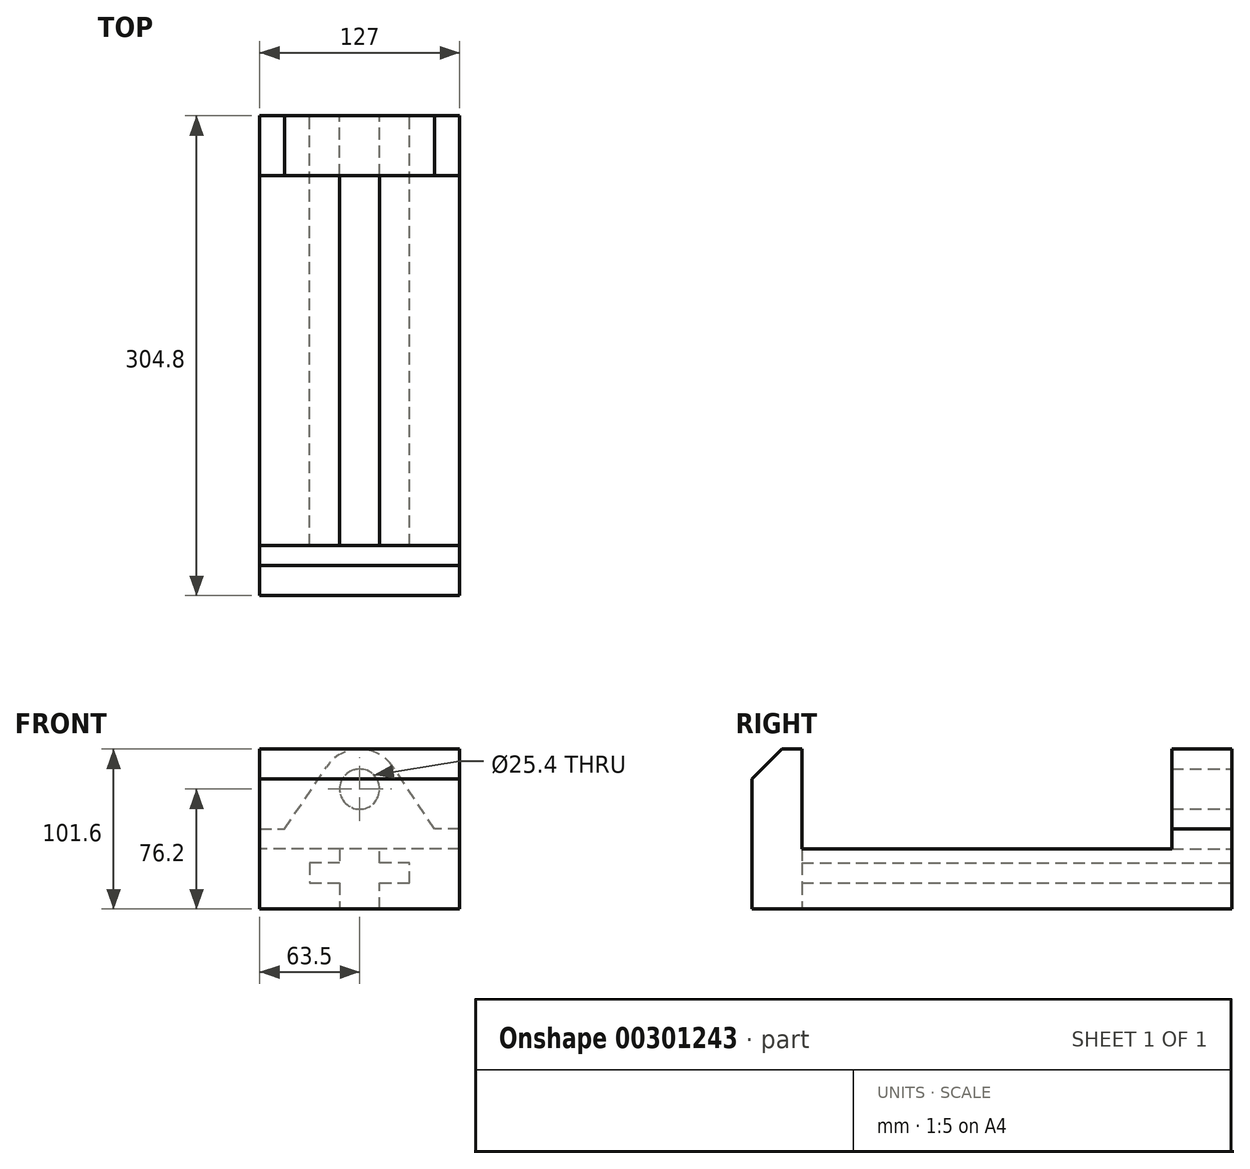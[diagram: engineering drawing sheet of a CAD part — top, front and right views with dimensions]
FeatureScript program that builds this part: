
annotation { "Feature Type Name" : "Feature", "Feature Type Description" : "" }
export const myFeature = defineFeature(function(context is Context, id is Id, definition is map)
    precondition{}
    {
        {
            var Q0;
            Q0=qCreatedBy(makeId("Right.planeOp"),FACE);
            var sketch = newSketch(context, id + "F0", { "sketchPlane" : qUnion([Q0])});
            skLineSegment(sketch, "E0", {"start": v(0, 0) * mm, "end": v(0, 101.6) * mm});
            skLineSegment(sketch, "E1", {"start": v(0, 101.6) * mm, "end": v(31.75, 101.6) * mm});
            skLineSegment(sketch, "E2", {"start": v(31.75, 101.6) * mm, "end": v(31.75, 38.1) * mm});
            skLineSegment(sketch, "E3", {"start": v(31.75, 38.1) * mm, "end": v(266.7, 38.1) * mm});
            skLineSegment(sketch, "E4", {"start": v(266.7, 38.1) * mm, "end": v(266.7, 101.6) * mm});
            skLineSegment(sketch, "E5", {"start": v(266.7, 101.6) * mm, "end": v(304.8, 101.6) * mm});
            skLineSegment(sketch, "E6", {"start": v(304.8, 101.6) * mm, "end": v(304.8, 0) * mm});
            skLineSegment(sketch, "E7", {"start": v(304.8, 0) * mm, "end": v(0, 0) * mm});
            skSolve(sketch);
        }
        {
            var Q0;
            Q0 = qSketchRegion(id + "F0", true);
            extrude(context, id + "F1", {"entities" : qUnion([Q0]), "endBound" : BoundingType.SYMMETRIC, "depth" : 127 * mm});
        }
        {
            var Q0;
            Q0=makeQuery(id+"F1.opExtrude","SWEPT_FACE",FACE,{"disambiguationData":[OSD([sQuery(id+"F0.wireOp",EDGE,"E6")])]});
            var sketch = newSketch(context, id + "F2", { "sketchPlane" : qUnion([Q0])});
            skLineSegment(sketch, "E8", {"start": v(-63.5, 50.8) * mm, "end": v(-47.63, 50.8) * mm});
            skLineSegment(sketch, "E9", {"start": v(-47.63, 50.8) * mm, "end": v(-21.1, 90.35) * mm});
            skLineSegment(sketch, "E10", {"start": v(63.5, 50.8) * mm, "end": v(47.63, 50.8) * mm});
            skPoint(sketch, "E10.endSnap0", {"position": v(63.5, 50.8) * mm});
            skLineSegment(sketch, "E11", {"start": v(47.63, 50.8) * mm, "end": v(21.1, 90.35) * mm});
            skArc(sketch, "E12", {"start": v(-21.1, 90.35) * mm, "mid": v(0, 101.6) * mm, "end": v(21.1, 90.35) * mm});
            skCircle(sketch, "E13", {"center": v(0, 76.2) * mm, "radius": 12.7 * mm});
            skLineSegment(sketch, "E14", {"start": v(-12.7, 0) * mm, "end": v(-12.7, 16.5) * mm});
            skLineSegment(sketch, "E15", {"start": v(-12.7, 16.5) * mm, "end": v(-31.75, 16.5) * mm});
            skLineSegment(sketch, "E16", {"start": v(-31.75, 16.5) * mm, "end": v(-31.75, 29.2) * mm});
            skLineSegment(sketch, "E17", {"start": v(-31.75, 29.2) * mm, "end": v(-12.7, 29.2) * mm});
            skLineSegment(sketch, "E18", {"start": v(-12.7, 29.2) * mm, "end": v(-12.7, 38.1) * mm});
            skLineSegment(sketch, "E19", {"start": v(-12.7, 38.1) * mm, "end": v(12.7, 38.1) * mm});
            skLineSegment(sketch, "E20", {"start": v(12.7, 38.1) * mm, "end": v(12.7, 29.2) * mm});
            skLineSegment(sketch, "E21", {"start": v(12.7, 29.2) * mm, "end": v(31.75, 29.2) * mm});
            skLineSegment(sketch, "E22", {"start": v(31.75, 29.2) * mm, "end": v(31.75, 16.5) * mm});
            skLineSegment(sketch, "E23", {"start": v(31.75, 16.5) * mm, "end": v(12.7, 16.5) * mm});
            skLineSegment(sketch, "E24", {"start": v(12.7, 16.5) * mm, "end": v(12.7, 0) * mm});
            skLineSegment(sketch, "E25", {"start": v(12.7, 0) * mm, "end": v(-12.7, 0) * mm});
            skLineSegment(sketch, "E26", {"start": v(-12.7, 0) * mm, "end": v(12.7, 0) * mm});
            skSolve(sketch);
        }
        {
            var Q0;
            {var subQ7=sQuery(id+"F2.wireOp",EDGE,"E8");Q0=makeQuery(id+"F2.imprint","IMPRINT",FACE,{"disambiguationData":[TD([[makeQuery(id+"F2.imprint","IMPRINT",EDGE,{"derivedFrom":subQ7}),1.0]])]});}
            var Q1;
            {var subQ7=sQuery(id+"F2.wireOp",EDGE,"E10");Q1=makeQuery(id+"F2.imprint","IMPRINT",FACE,{"disambiguationData":[TD([[makeQuery(id+"F2.imprint","IMPRINT",EDGE,{"derivedFrom":subQ7}),-1.0]])]});}
            var Q2;
            Q2=makeQuery(id+"F2.imprint","IMPRINT",FACE,{"disambiguationData":[TD([[makeQuery(id+"F2.imprint","IMPRINT",EDGE,{"derivedFrom":sQuery(id+"F2.wireOp",EDGE,"E13")}),1.0]])]});
            extrude(context, id + "F3", {"entities" : qUnion([Q0, Q1, Q2]), "operationType" : NewBodyOperationType.REMOVE, "oppositeDirection" : true, "depth" : 50.8 * mm});
        }
        {
            var Q0;
            Q0=makeQuery(id+"F2.imprint","IMPRINT",FACE,{"disambiguationData":[TD([[makeQuery(id+"F2.imprint","IMPRINT",EDGE,{"derivedFrom":sQuery(id+"F2.wireOp",EDGE,"E14")}),-1.0]])]});
            var Q1;
            Q1=makeQuery(id+"F1.opExtrude","SWEPT_FACE",FACE,{"disambiguationData":[OSD([sQuery(id+"F0.wireOp",EDGE,"E2")])]});
            extrude(context, id + "F4", {"entities" : qUnion([Q0]), "operationType" : NewBodyOperationType.REMOVE, "endBound" : BoundingType.UP_TO_SURFACE, "oppositeDirection" : true, "endBoundEntityFace" : qUnion([Q1]), "depth" : 25.4 * mm});
        }
        {
            var Q0;
            Q0=makeQuery(id+"F1.opExtrude","SWEPT_EDGE",EDGE,{"disambiguationData":[OSD([sQuery(id+"F0.wireOp",EDGE,"E0"),sQuery(id+"F0.wireOp",EDGE,"E1")])]});
            chamfer(context, id + "F5", {"entities" : qUnion([Q0]), "chamferType" : ChamferType.TWO_OFFSETS, "width1" : 19.05 * mm, "oppositeDirection" : false, "width2" : 19.05 * mm, "tangentPropagation" : true});
        }
    });
